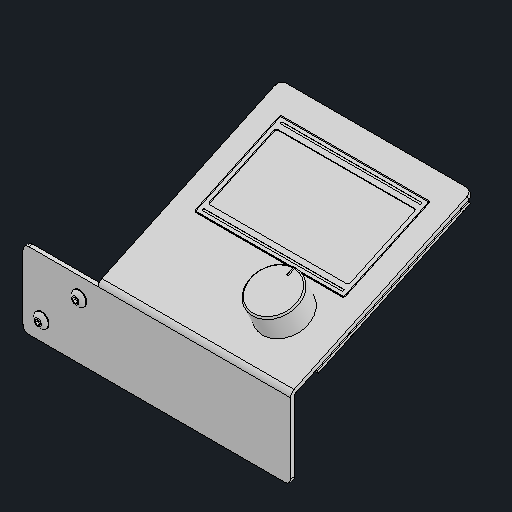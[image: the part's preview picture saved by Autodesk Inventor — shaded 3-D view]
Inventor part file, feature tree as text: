
AUTODESK INVENTOR PART (.ipt)
format: ipt  version: 2024.2 (Build 282272000, 272)  size: 1,350,144 bytes
history: native  units: mm
features: other x35, mirror x3, fillet x1, chamfer x1
ambient origin geometry x8: Origin, YZ Plane, XZ Plane, XY Plane, X Axis, Y Axis, Z Axis, Center Point
bodies: Body1 (feature_tree), Body2 (feature_tree), Body3 (feature_tree), Body4 (feature_tree), Body5 (feature_tree), Body6 (feature_tree), Body7 (feature_tree), Body8 (feature_tree), Body9 (feature_tree), Body10 (feature_tree), Body11 (feature_tree), Body12 (feature_tree), Body13 (feature_tree), Body14 (feature_tree), Body15 (feature_tree), Body16 (feature_tree), Body17 (feature_tree), Body18 (feature_tree), Body19 (feature_tree), Body20 (feature_tree)
feature tree (40):
  other  "솔리드1"
  other  "솔리드2"
  other  "솔리드3"
  other  "솔리드4"
  other  "솔리드5"
  other  "솔리드6"
  other  "솔리드7"
  other  "솔리드8"
  other  "솔리드9"
  other  "솔리드10"
  other  "솔리드11"
  other  "솔리드12"
  other  "솔리드13"
  other  "솔리드14"
  other  "솔리드15"
  other  "솔리드16"
  other  "솔리드17"
  other  "솔리드18"
  other  "솔리드19"
  other  "솔리드20"
  other  "Boss-Extrude2-pcb"
  other  "Boss-Extrude3-pcb"
  other  "M3x0.5 Tapped Hole1-pcb-screw-bosses"
  other  "Body-Move_Copy1-pcb-screw-bosses"
  mirror  "Mirror1-pcb-screw-bosses[1]"
  mirror  "Mirror1-pcb-screw-bosses[2]"
  other  "Body-Move_Copy2-pcb[1]"
  other  "Body-Move_Copy2-pcb[2]"
  other  "Cut-Extrude5-pcb"
  fillet  "Fillet14-display-frame"  [1 undecoded]
  other  "Boss-Extrude13-display-glass"
  chamfer  "Chamfer2-knob"  [1 undecoded]
  other  "_bhcs-M4_-_ThdSchPat_"
  other  "_bhcs-M4_-_ThdSchPat_:1"
  other  "_t-slot-nut_-_M4x0.7 Tapped Hole1_"
  other  "_t-slot-nut_-_M4x0.7 Tapped Hole1_:1"
  other  "_bhcs-M3_-_ThdSchPat_"
  mirror  "Mirror1"
  other  "Body-Move_Copy11[1]"
  other  "Body-Move_Copy11[2]"
note: 2 required parameter values undecoded (feature->parameter linkage not recoverable at this tier; creation-order binding heuristic only, values carry confidence <= 0.55)
